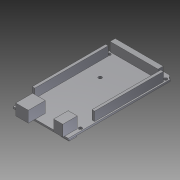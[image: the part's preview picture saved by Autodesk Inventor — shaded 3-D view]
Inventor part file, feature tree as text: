
AUTODESK INVENTOR PART (.ipt)
format: ipt  version: 2011 SP2 (Build 150309200, 309)  size: 226,816 bytes
history: native  units: mm
features: extrude x6, projected_geometry x5, sketch x3
ambient origin geometry x8: Origin, YZ Plane, XZ Plane, XY Plane, X Axis, Y Axis, Z Axis, Center Point
bodies: Solid1 (feature_tree)
feature tree (14):
  extrude  "Extrusion1"  Depth=1.7mm
  sketch  "Sketch3"  dims[d2=53.3mm d3=0.0mm d23=9.1mm]
  extrude  "Extrusion3"  Depth=9.1mm
  extrude  "Extrusion9"  Depth=16.4mm
  extrude  "Extrusion10"  Depth=12.2mm
  sketch  "Sketch7"  dims[d24=9.75mm d25=16.4mm d26=12.2mm d27=8.8mm d28=14.0mm d29=12.4mm d30=1.7mm d31=10.8mm d32=0.0mm d44=3.0mm d45=3.4mm d46=3.0mm d47=3.0mm d48=1.4mm d49=4.0mm d50=35.12mm d51=12.0mm d52=3.3mm d53=3.3mm d54=3.3mm d55=3.3mm d56=3.3mm d57=3.3mm d58=0.9mm d59=3.6mm d60=6.9mm d61=0.9mm d62=0.9mm d63=0.9mm d64=13.6mm d66=12.6mm d67=34.0mm d69=34.0mm d70=6.0mm d71=16.2mm d72=71.0mm d73=0.25mm d74=2.5mm d75=1.25mm d76=66.5mm d77=2.5mm d78=1.25mm d79=1.8mm d80=5.0mm d81=46.4mm d82=1.1mm d83=0.95mm d84=10.0mm d85=0.0mm d86=8.7mm d87=0.0mm d110=1.0mm d111=1.0mm d112=1.0mm d113=1.5mm d114=1.0mm d115=1.3mm d116=0.0mm d117=2.5mm d118=0.0mm]
  extrude  "Extrusion12"  Depth=8.8mm
  extrude  "Extrusion13"  Depth=14.0mm
  sketch  "Sketch1"  dims[d0=102.0mm d1=1.7mm]
  projected_geometry  "Projected Loop1"
  projected_geometry  "Projected Loop2"
  projected_geometry  "Projected Loop3"
  projected_geometry  "Projected Loop4"
  projected_geometry  "Projected Loop5"
